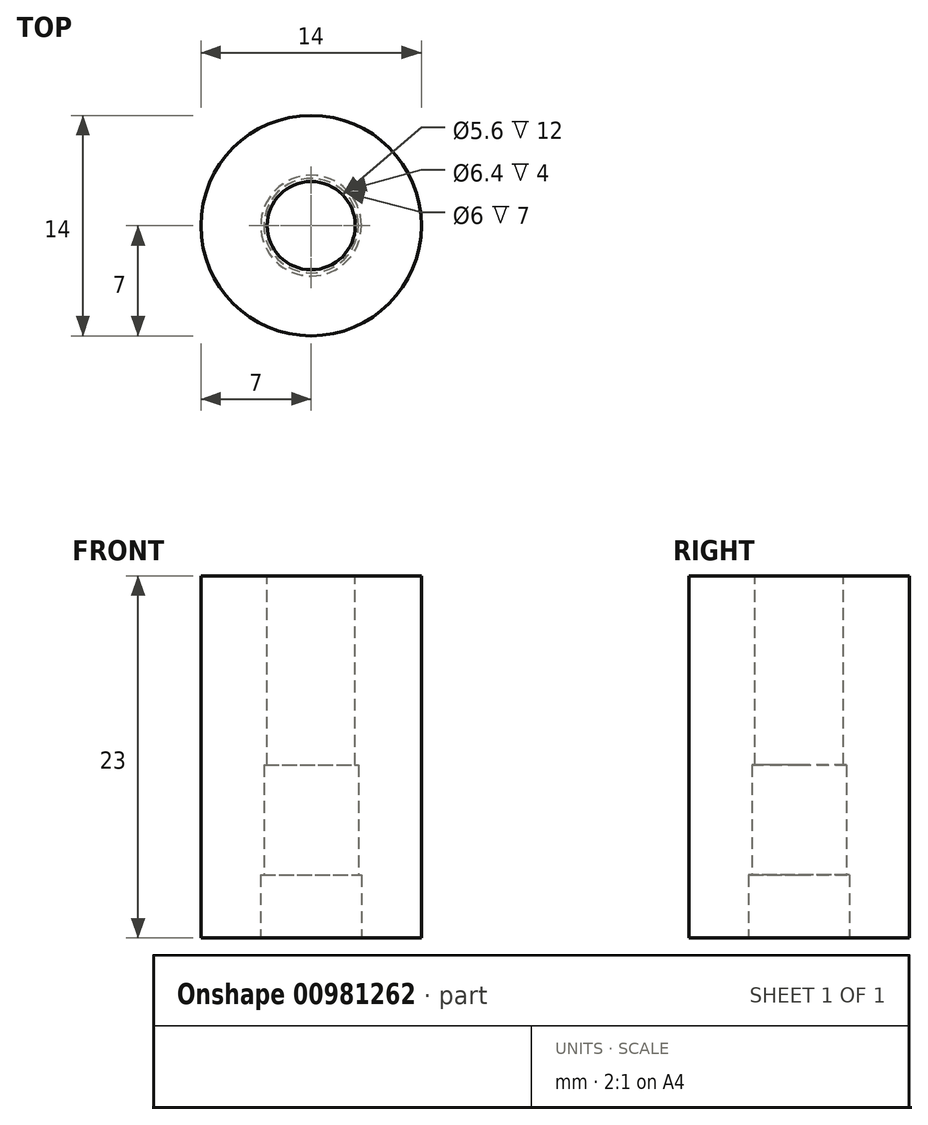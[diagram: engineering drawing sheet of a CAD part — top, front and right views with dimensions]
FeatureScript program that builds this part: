
annotation { "Feature Type Name" : "Feature", "Feature Type Description" : "" }
export const myFeature = defineFeature(function(context is Context, id is Id, definition is map)
    precondition{}
    {
        {
            var Q0;
            Q0=qCreatedBy(makeId("Top.planeOp"),FACE);
            var sketch = newSketch(context, id + "F0", { "sketchPlane" : qUnion([Q0])});
            skCircle(sketch, "E0", {"center": v(0, 0) * mm, "radius": 7 * mm});
            skSolve(sketch);
        }
        {
            var Q0;
            Q0=makeQuery(id+"F0.imprint","IMPRINT",FACE,{"disambiguationData":[TD([[makeQuery(id+"F0.imprint","IMPRINT",EDGE,{"derivedFrom":sQuery(id+"F0.wireOp",EDGE,"E0")}),1.0]])]});
            extrude(context, id + "F1", {"entities" : qUnion([Q0]), "depth" : 23 * mm, "offsetDistance" : 25 * mm});
        }
        {
            var Q0;
            Q0=makeQuery(id+"F1.opExtrude","CAP_FACE",FACE,{"disambiguationData":[OSD([sQuery(id+"F0.wireOp",EDGE,"E0")])],"isStart":false});
            var sketch = newSketch(context, id + "F2", { "sketchPlane" : qUnion([Q0])});
            skCircle(sketch, "E1", {"center": v(0, 0) * mm, "radius": 2.8 * mm});
            skSolve(sketch);
        }
        {
            var Q0;
            Q0=makeQuery(id+"F2.imprint","IMPRINT",FACE,{"disambiguationData":[TD([[makeQuery(id+"F2.imprint","IMPRINT",EDGE,{"derivedFrom":sQuery(id+"F2.wireOp",EDGE,"E1")}),1.0]])]});
            extrude(context, id + "F3", {"entities" : qUnion([Q0]), "operationType" : NewBodyOperationType.REMOVE, "endBound" : BoundingType.THROUGH_ALL, "oppositeDirection" : true, "depth" : 15 * mm, "offsetDistance" : 25 * mm});
        }
        {
            var Q0;
            Q0=makeQuery(id+"F1.opExtrude","CAP_FACE",FACE,{"disambiguationData":[OSD([sQuery(id+"F0.wireOp",EDGE,"E0")])],"isStart":true});
            var sketch = newSketch(context, id + "F4", { "sketchPlane" : qUnion([Q0])});
            skCircle(sketch, "E2", {"center": v(0, 0) * mm, "radius": 3.2 * mm});
            skSolve(sketch);
        }
        {
            var Q0;
            Q0=makeQuery(id+"F4.imprint","IMPRINT",FACE,{"disambiguationData":[TD([[makeQuery(id+"F4.imprint","IMPRINT",EDGE,{"derivedFrom":sQuery(id+"F4.wireOp",EDGE,"E2")}),1.0]])]});
            extrude(context, id + "F5", {"entities" : qUnion([Q0]), "operationType" : NewBodyOperationType.REMOVE, "oppositeDirection" : true, "depth" : 4 * mm, "offsetDistance" : 25 * mm});
        }
        {
            var Q0;
            Q0=makeQuery(id+"F5.boolean.opBoolean","COPY",FACE,{"derivedFrom":makeQuery(id+"F5.opExtrude","CAP_FACE",FACE,{"disambiguationData":[OSD([sQuery(id+"F4.wireOp",EDGE,"E2")])],"isStart":false})});
            var sketch = newSketch(context, id + "F6", { "sketchPlane" : qUnion([Q0])});
            skCircle(sketch, "E3", {"center": v(0, 0) * mm, "radius": 3 * mm});
            skSolve(sketch);
        }
        {
            var Q0;
            Q0 = qSketchRegion(id + "F6", true);
            extrude(context, id + "F7", {"entities" : qUnion([Q0]), "operationType" : NewBodyOperationType.REMOVE, "oppositeDirection" : true, "depth" : 7 * mm, "offsetDistance" : 25 * mm});
        }
    });
